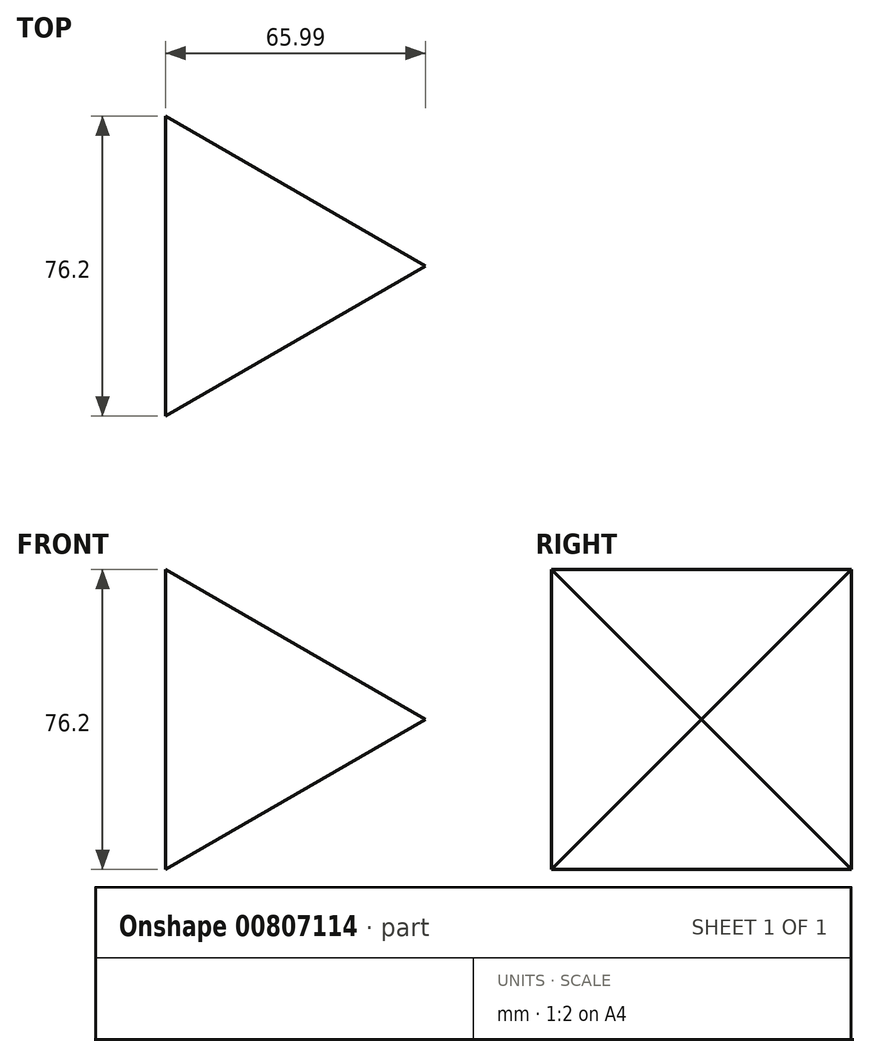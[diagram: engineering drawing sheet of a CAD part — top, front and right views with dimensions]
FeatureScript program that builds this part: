
annotation { "Feature Type Name" : "Feature", "Feature Type Description" : "" }
export const myFeature = defineFeature(function(context is Context, id is Id, definition is map)
    precondition{}
    {
        {
            var Q0;
            Q0=qCreatedBy(makeId("Right.planeOp"),FACE);
            var sketch = newSketch(context, id + "F0", { "sketchPlane" : qUnion([Q0])});
            skLineSegment(sketch, "E0.bottom", {"start": v(82.56, -14.7) * mm, "end": v(6.36, -14.7) * mm});
            skLineSegment(sketch, "E0.top", {"start": v(82.56, 61.5) * mm, "end": v(6.36, 61.5) * mm});
            skLineSegment(sketch, "E0.left", {"start": v(82.56, -14.7) * mm, "end": v(82.56, 61.5) * mm});
            skLineSegment(sketch, "E0.right", {"start": v(6.36, -14.7) * mm, "end": v(6.36, 61.5) * mm});
            skSolve(sketch);
        }
        {
            var Q0;
            Q0 = qSketchRegion(id + "F0", true);
            extrude(context, id + "F1", {"entities" : qUnion([Q0]), "depth" : 81.8 * mm, "offsetDistance" : 25.4 * mm, "hasDraft" : true, "draftAngle" : 30 * degree, "draftPullDirection" : true});
        }
    });
